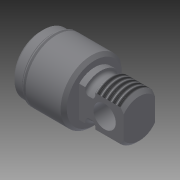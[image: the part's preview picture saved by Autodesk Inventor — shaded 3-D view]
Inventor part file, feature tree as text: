
AUTODESK INVENTOR PART (.ipt)
format: ipt  version: 2014 (Build 180170000, 170)  size: 281,600 bytes
history: native  units: in
note: dims shown in document units (in); Inventor stores cm internally (conversion verified against a paired STEP export)
features: other x91, sketch x9, revolve x7, thread x2, hole x1, extrude x1
ambient origin geometry x8: Origin, YZ Plane, XZ Plane, XY Plane, X Axis, Y Axis, Z Axis, Center Point
bodies: Solid1 (feature_tree)
feature tree (111):
  revolve  "Revolution1"  Angle=360.0deg
  hole  "Hole1"  [1 undecoded]
  revolve  "Revolution2"  [1 undecoded]
  revolve  "Revolution3"  Angle=360.0deg
  revolve  "Revolution4"  [1 undecoded]
  revolve  "Revolution5"  [1 undecoded]
  thread  "Thread1"  [1 undecoded]
  extrude  "Extrusion1"  [1 undecoded]
  revolve  "Revolution6"  [1 undecoded]
  revolve  "Revolution7"  [1 undecoded]
  thread  "Thread2"  [1 undecoded]
  other  "aa2_XY"
  other  "aa2_YZ"
  other  "aa2_ZX"
  other  "aa2_X"
  other  "aa2_Y"
  other  "aa2_Z"
  other  "aa2_Center"
  other  "mm1_XY"
  other  "mm1_YZ"
  other  "mm1_ZX"
  other  "mm1_X"
  other  "mm1_Y"
  other  "mm1_Z"
  other  "mm1_Center"
  other  "mm2_XY"
  other  "mm2_YZ"
  other  "mm2_ZX"
  other  "mm2_X"
  other  "mm2_Y"
  other  "mm2_Z"
  other  "mm2_Center"
  other  "nn1_XY"
  other  "nn1_YZ"
  other  "nn1_ZX"
  other  "nn1_X"
  other  "nn1_Y"
  other  "nn1_Z"
  other  "nn1_Center"
  other  "nn2_XY"
  other  "nn2_YZ"
  other  "nn2_ZX"
  other  "nn2_X"
  other  "nn2_Y"
  other  "nn2_Z"
  other  "nn2_Center"
  other  "p1_XY"
  other  "p1_YZ"
  other  "p1_ZX"
  other  "p1_X"
  other  "p1_Y"
  other  "p1_Z"
  other  "p1_Center"
  other  "q2_XY"
  other  "q2_YZ"
  other  "q2_ZX"
  other  "q2_X"
  other  "q2_Y"
  other  "q2_Z"
  other  "q2_Center"
  other  "r1_XY"
  other  "r1_YZ"
  other  "r1_ZX"
  other  "r1_X"
  other  "r1_Y"
  other  "r1_Z"
  other  "r1_Center"
  other  "r2_XY"
  other  "r2_YZ"
  other  "r2_ZX"
  other  "r2_X"
  other  "r2_Y"
  other  "r2_Z"
  other  "r2_Center"
  other  "rear_head_XY"
  other  "rear_head_YZ"
  other  "rear_head_ZX"
  other  "rear_head_X"
  other  "rear_head_Y"
  other  "rear_head_Z"
  other  "rear_head_Center"
  other  "to_bushing_XY"
  other  "to_bushing_YZ"
  other  "to_bushing_ZX"
  other  "to_bushing_X"
  other  "to_bushing_Y"
  other  "to_bushing_Z"
  other  "to_bushing_Center"
  other  "to_mounting_bracket_xp_XY"
  other  "to_mounting_bracket_xp_YZ"
  other  "to_mounting_bracket_xp_ZX"
  other  "to_mounting_bracket_xp_X"
  other  "to_mounting_bracket_xp_Y"
  other  "to_mounting_bracket_xp_Z"
  other  "to_mounting_bracket_xp_Center"
  other  "to_pivot_bracket_XY"
  other  "to_pivot_bracket_YZ"
  other  "to_pivot_bracket_ZX"
  other  "to_pivot_bracket_X"
  other  "to_pivot_bracket_Y"
  other  "to_pivot_bracket_Z"
  other  "to_pivot_bracket_Center"
  sketch  "Sketch_1"  dims[d0=360.0deg]
  sketch  "Sketch2"  dims[d1=0.375in d2=0.75in d3=0.435in d4=0.25in d5=90.0deg d6=0.188in d7=0.0in d8=360.0deg]
  sketch  "Sketch_6"  dims[d9=360.0deg d10=360.0deg]
  sketch  "Sketch_9"  dims[d11=360.0deg d12=0.2472in d13=0.0in]
  sketch  "Sketch_23"
  sketch  "Sketch_12"  dims[d14=0.437in d15=0.0in d16=360.0deg]
  sketch  "Sketch_13"  dims[d17=360.0deg d18=0.1686in d19=0.0in]
  sketch  "Sketch_21"
  sketch  "Sketch_17"
note: 9 required parameter values undecoded (feature->parameter linkage not recoverable at this tier; creation-order binding heuristic only, values carry confidence <= 0.55)